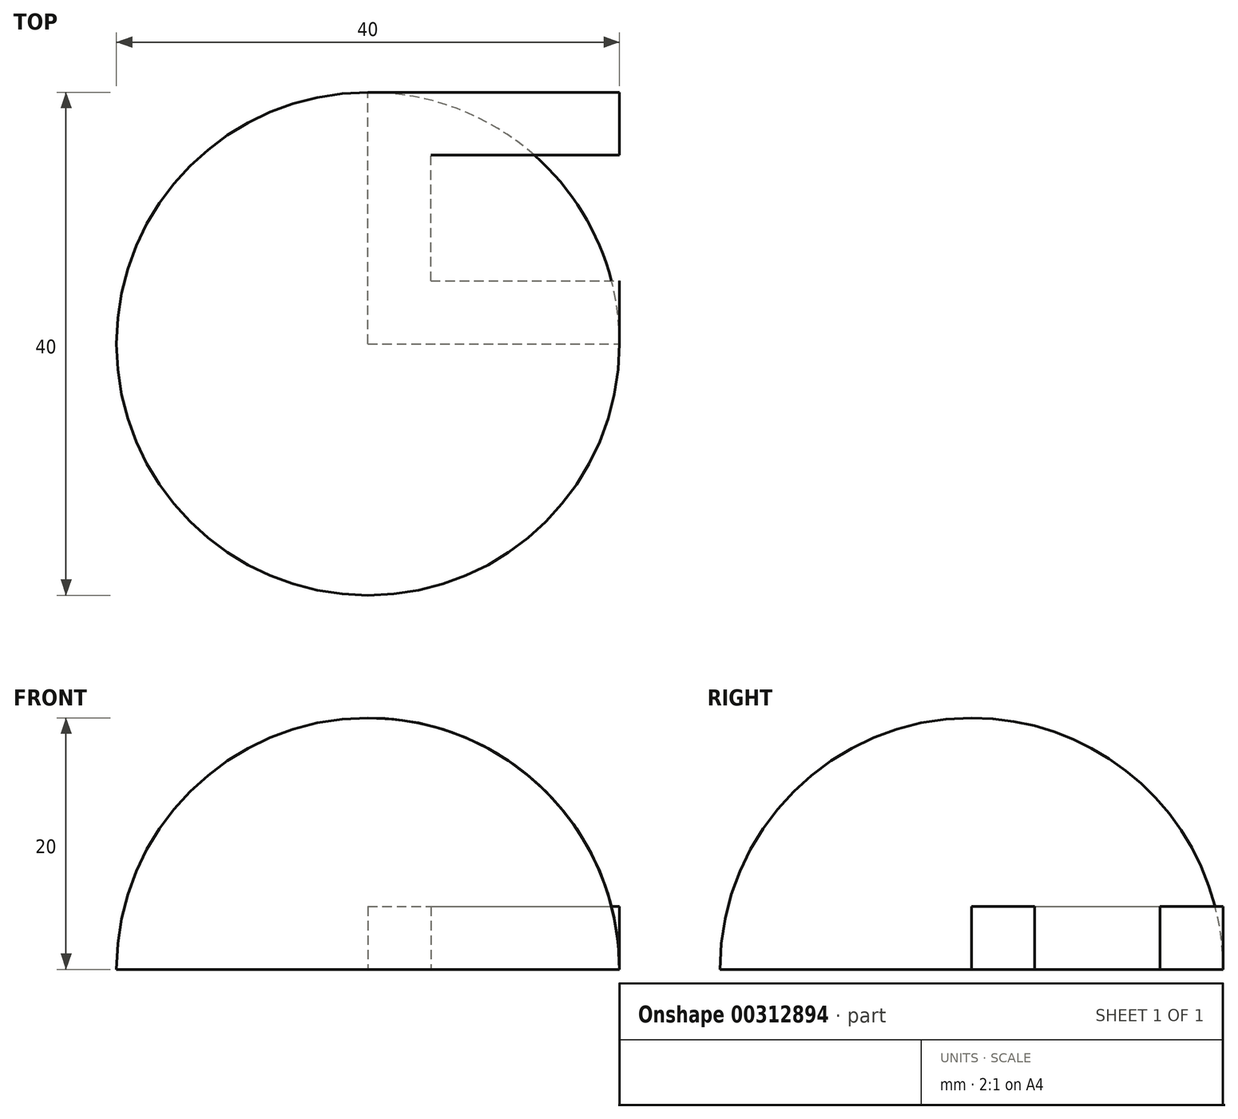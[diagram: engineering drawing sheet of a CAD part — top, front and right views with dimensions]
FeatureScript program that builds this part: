
annotation { "Feature Type Name" : "Feature", "Feature Type Description" : "" }
export const myFeature = defineFeature(function(context is Context, id is Id, definition is map)
    precondition{}
    {
        {
            var Q0;
            Q0=qCreatedBy(makeId("Top.planeOp"),FACE);
            var sketch = newSketch(context, id + "F0", { "sketchPlane" : qUnion([Q0])});
            skLineSegment(sketch, "E0.bottom", {"start": v(0, 0) * mm, "end": v(5, 0) * mm});
            skLineSegment(sketch, "E0.top", {"start": v(0, 20) * mm, "end": v(5, 20) * mm});
            skLineSegment(sketch, "E0.left", {"start": v(0, 0) * mm, "end": v(0, 20) * mm});
            skLineSegment(sketch, "E0.right", {"start": v(5, 0) * mm, "end": v(5, 20) * mm});
            skLineSegment(sketch, "E1.bottom", {"start": v(0, 20) * mm, "end": v(20, 20) * mm});
            skLineSegment(sketch, "E1.top", {"start": v(0, 15) * mm, "end": v(20, 15) * mm});
            skLineSegment(sketch, "E1.left", {"start": v(0, 20) * mm, "end": v(0, 15) * mm});
            skLineSegment(sketch, "E1.right", {"start": v(20, 20) * mm, "end": v(20, 15) * mm});
            skLineSegment(sketch, "E2.bottom", {"start": v(0, 5) * mm, "end": v(20, 5) * mm});
            skLineSegment(sketch, "E2.top", {"start": v(0, 0) * mm, "end": v(20, 0) * mm});
            skLineSegment(sketch, "E2.left", {"start": v(0, 5) * mm, "end": v(0, 0) * mm});
            skLineSegment(sketch, "E2.right", {"start": v(20, 5) * mm, "end": v(20, 0) * mm});
            skSolve(sketch);
        }
        {
            var Q0;
            Q0 = qSketchRegion(id + "F0", true);
            extrude(context, id + "F1", {"entities" : qUnion([Q0]), "depth" : 5 * mm, "offsetDistance" : 25 * mm});
        }
        {
            var Q0;
            Q0=qCreatedBy(makeId("Front.planeOp"),FACE);
            var sketch = newSketch(context, id + "F2", { "sketchPlane" : qUnion([Q0])});
            skLineSegment(sketch, "E3", {"start": v(0, 0) * mm, "end": v(0, 20) * mm});
            skArc(sketch, "E4", {"start": v(20, 0) * mm, "mid": v(14.14, 14.14) * mm, "end": v(0, 20) * mm});
            skLineSegment(sketch, "E5", {"start": v(0, 0) * mm, "end": v(20, 0) * mm});
            skSolve(sketch);
        }
        {
            var Q0;
            Q0 = qSketchRegion(id + "F2", true);
            var Q1;
            Q1=sQuery(id+"F2.wireOp",EDGE,"E3");
            revolve(context, id + "F3", {"surfaceOperationType" : NewSurfaceOperationType.NEW, "entities" : qUnion([Q0]), "axis" : qUnion([Q1]), "revolveType" : RevolveType.FULL});
        }
    });
